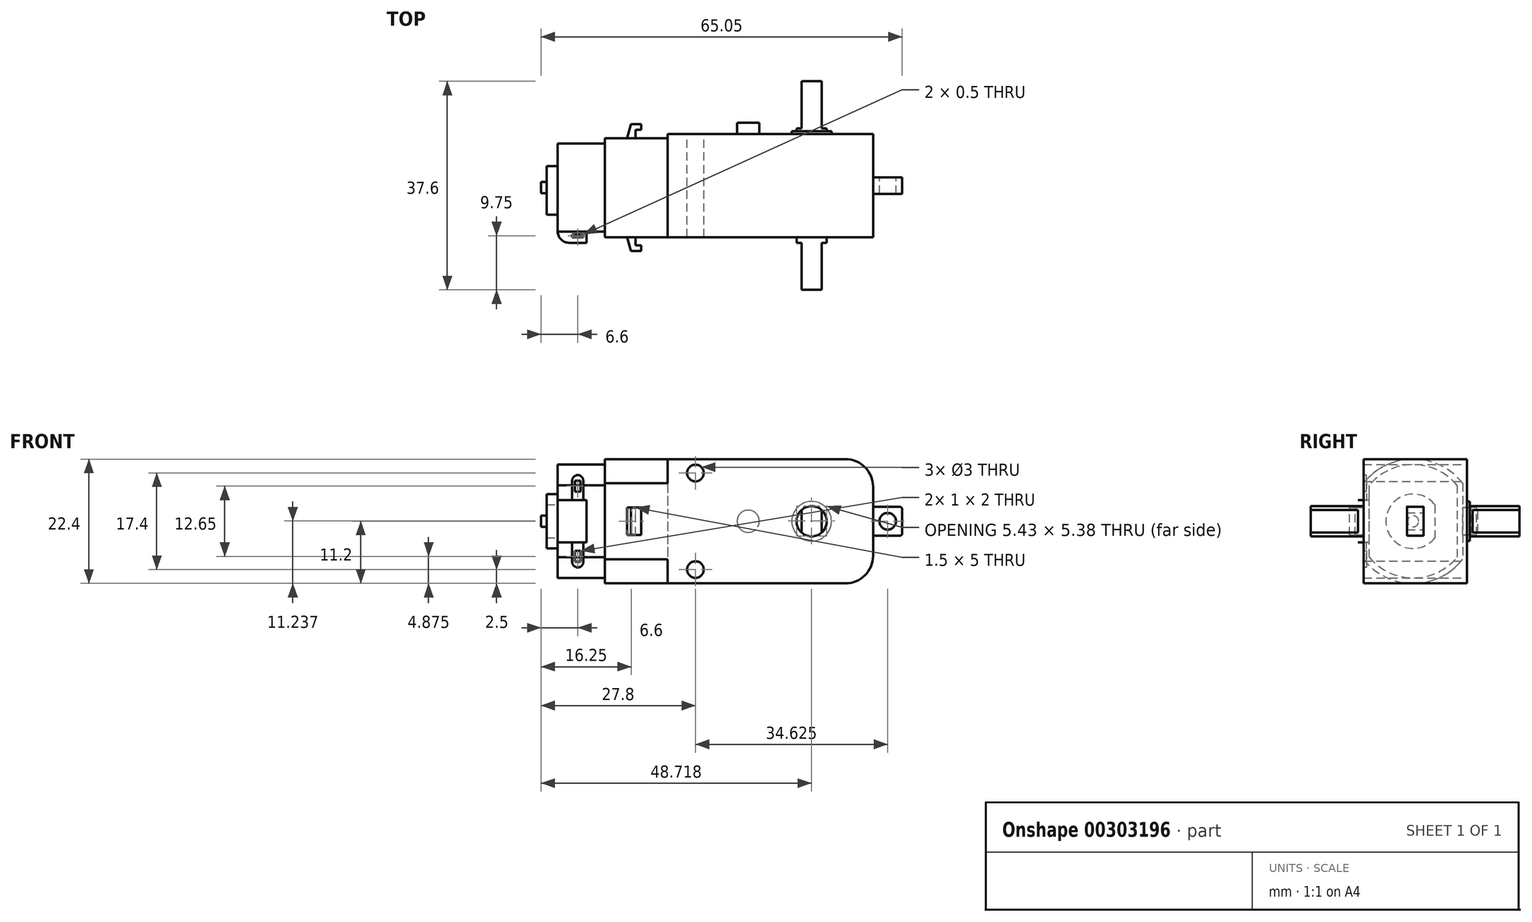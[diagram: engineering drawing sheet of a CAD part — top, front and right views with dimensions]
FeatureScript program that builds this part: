
annotation { "Feature Type Name" : "Feature", "Feature Type Description" : "" }
export const myFeature = defineFeature(function(context is Context, id is Id, definition is map)
    precondition{}
    {
        {
            var Q0;
            Q0=qCreatedBy(makeId("Top.planeOp"),FACE);
            var sketch = newSketch(context, id + "F0", { "sketchPlane" : qUnion([Q0])});
            skLineSegment(sketch, "E0.bottom", {"start": v(18.5, -9.3) * mm, "end": v(-18.5, -9.3) * mm});
            skLineSegment(sketch, "E0.top", {"start": v(18.5, 9.3) * mm, "end": v(-18.5, 9.3) * mm});
            skLineSegment(sketch, "E0.left", {"start": v(18.5, -9.3) * mm, "end": v(18.5, 9.3) * mm});
            skLineSegment(sketch, "E0.right", {"start": v(-18.5, -9.3) * mm, "end": v(-18.5, 9.3) * mm});
            skPoint(sketch, "E0.middle", {"position": v(0, 0) * mm});
            skSolve(sketch);
        }
        {
            var Q0;
            Q0 = qSketchRegion(id + "F0", true);
            extrude(context, id + "F1", {"entities" : qUnion([Q0]), "depth" : 22.4 * mm});
        }
        {
            var Q0;
            Q0=makeQuery(id+"F1.opExtrude","SWEPT_FACE",FACE,{"disambiguationData":[OSD([sQuery(id+"F0.wireOp",EDGE,"E0.right")])]});
            var sketch = newSketch(context, id + "F2", { "sketchPlane" : qUnion([Q0])});
            skLineSegment(sketch, "E1.0.1", {"start": v(9.3, 4.35) * mm, "end": v(9.3, 18.05) * mm});
            skLineSegment(sketch, "E1.0.2", {"start": v(0.38, 22.4) * mm, "end": v(0.38, 22.4) * mm});
            skLineSegment(sketch, "E1.0.3", {"start": v(-9.3, 22.4) * mm, "end": v(-9.3, 0) * mm, "construction": true});
            skLineSegment(sketch, "E2", {"start": v(-8.55, 18.05) * mm, "end": v(-8.55, 4.35) * mm});
            skLineSegment(sketch, "E3", {"start": v(-8.55, 11.2) * mm, "end": v(9.3, 11.2) * mm, "construction": true});
            skLineSegment(sketch, "E4", {"start": v(0.38, 11.2) * mm, "end": v(0.38, 22.4) * mm, "construction": true});
            skArc(sketch, "E5", {"start": v(9.3, 18.05) * mm, "mid": v(0.38, 22.4) * mm, "end": v(-8.55, 18.05) * mm});
            skArc(sketch, "E6.MirrorC", {"start": v(9.3, 4.35) * mm, "mid": v(0.38, 0) * mm, "end": v(-8.55, 4.35) * mm});
            skPoint(sketch, "E7.orphan", {"position": v(-8.55, 0) * mm});
            skPoint(sketch, "E8.orphan", {"position": v(9.3, 0) * mm});
            skPoint(sketch, "E9.orphan", {"position": v(9.3, 22.4) * mm});
            skPoint(sketch, "E10.orphan", {"position": v(-8.55, 22.4) * mm});
            skLineSegment(sketch, "E11", {"start": v(0.38, 11.2) * mm, "end": v(0.38, 0) * mm, "construction": true});
            skSolve(sketch);
        }
        {
            var Q0;
            Q0 = qSketchRegion(id + "F2", true);
            extrude(context, id + "F3", {"entities" : qUnion([Q0]), "operationType" : NewBodyOperationType.ADD, "depth" : 11.3 * mm});
        }
        {
            var Q0;
            Q0=makeQuery(id+"F3.opExtrude","CAP_FACE",FACE,{"disambiguationData":[OSD([sQuery(id+"F2.wireOp",EDGE,"E1.0.1"),sQuery(id+"F2.wireOp",EDGE,"E2"),sQuery(id+"F2.wireOp",EDGE,"E5"),sQuery(id+"F2.wireOp",EDGE,"E6.MirrorC")])],"isStart":false});
            var sketch = newSketch(context, id + "F4", { "sketchPlane" : qUnion([Q0])});
            skArc(sketch, "E12.0", {"start": v(-7.55, 4.7) * mm, "mid": v(0.38, 1) * mm, "end": v(8.3, 4.7) * mm});
            skLineSegment(sketch, "E12.1", {"start": v(-7.55, 17.7) * mm, "end": v(-7.55, 4.7) * mm});
            skArc(sketch, "E12.2", {"start": v(8.3, 17.7) * mm, "mid": v(0.38, 21.4) * mm, "end": v(-7.55, 17.7) * mm});
            skLineSegment(sketch, "E12.3", {"start": v(8.3, 4.7) * mm, "end": v(8.3, 17.7) * mm});
            skSolve(sketch);
        }
        {
            var Q0;
            Q0 = qSketchRegion(id + "F4", true);
            extrude(context, id + "F5", {"entities" : qUnion([Q0]), "operationType" : NewBodyOperationType.ADD, "depth" : 8.5 * mm});
        }
        {
            var Q0;
            Q0=makeQuery(id+"F5.opExtrude","CAP_FACE",FACE,{"disambiguationData":[OSD([sQuery(id+"F4.wireOp",EDGE,"E12.0"),sQuery(id+"F4.wireOp",EDGE,"E12.1"),sQuery(id+"F4.wireOp",EDGE,"E12.2"),sQuery(id+"F4.wireOp",EDGE,"E12.3")])],"isStart":false});
            var sketch = newSketch(context, id + "F6", { "sketchPlane" : qUnion([Q0])});
            skArc(sketch, "E13.0.0", {"start": v(-7.55, 4.7) * mm, "mid": v(0.38, 1) * mm, "end": v(8.3, 4.7) * mm, "construction": true});
            skLineSegment(sketch, "E13.0.1", {"start": v(8.3, 4.7) * mm, "end": v(8.3, 17.7) * mm, "construction": true});
            skArc(sketch, "E13.0.2", {"start": v(8.3, 17.7) * mm, "mid": v(0.38, 21.4) * mm, "end": v(-7.55, 17.7) * mm, "construction": true});
            skLineSegment(sketch, "E13.0.3", {"start": v(-7.55, 17.7) * mm, "end": v(-7.55, 4.7) * mm, "construction": true});
            skLineSegment(sketch, "E14", {"start": v(0.38, 11.07) * mm, "end": v(0.38, 11.33) * mm, "construction": true});
            skArc(sketch, "E15", {"start": v(-3.52, 8.23) * mm, "mid": v(5.28, 11.2) * mm, "end": v(-3.52, 14.17) * mm});
            skLineSegment(sketch, "E16", {"start": v(-3.52, 14.17) * mm, "end": v(-3.52, 8.23) * mm});
            skSolve(sketch);
        }
        {
            var Q0;
            Q0 = qSketchRegion(id + "F6", true);
            extrude(context, id + "F7", {"entities" : qUnion([Q0]), "operationType" : NewBodyOperationType.ADD, "depth" : 2 * mm});
        }
        {
            var Q0;
            Q0=makeQuery(id+"F7.opExtrude","CAP_FACE",FACE,{"disambiguationData":[OSD([sQuery(id+"F6.wireOp",EDGE,"E15"),sQuery(id+"F6.wireOp",EDGE,"E16")])],"isStart":false});
            var sketch = newSketch(context, id + "F8", { "sketchPlane" : qUnion([Q0])});
            skArc(sketch, "E17.0.0", {"start": v(-3.52, 8.23) * mm, "mid": v(5.28, 11.2) * mm, "end": v(-3.52, 14.17) * mm, "construction": true});
            skLineSegment(sketch, "E17.0.1", {"start": v(-3.52, 14.17) * mm, "end": v(-3.52, 8.23) * mm, "construction": true});
            skCircle(sketch, "E18", {"center": v(0.38, 11.2) * mm, "radius": 1 * mm});
            skSolve(sketch);
        }
        {
            var Q0;
            Q0 = qSketchRegion(id + "F8", true);
            extrude(context, id + "F9", {"entities" : qUnion([Q0]), "operationType" : NewBodyOperationType.ADD, "depth" : 1 * mm});
        }
        {
            var Q0;
            Q0=makeQuery(id+"F1.opExtrude","SWEPT_FACE",FACE,{"disambiguationData":[OSD([sQuery(id+"F0.wireOp",EDGE,"E0.top")])]});
            var sketch = newSketch(context, id + "F10", { "sketchPlane" : qUnion([Q0])});
            skLineSegment(sketch, "E19", {"start": v(-11, 22.4) * mm, "end": v(-11, 0) * mm, "construction": true});
            skLineSegment(sketch, "E20", {"start": v(-18.5, 11.2) * mm, "end": v(18.5, 11.2) * mm, "construction": true});
            skCircle(sketch, "E21", {"center": v(-7.42, 11.2) * mm, "radius": 3.58 * mm});
            skSolve(sketch);
        }
        {
            var Q0;
            Q0 = qSketchRegion(id + "F10", true);
            extrude(context, id + "F11", {"entities" : qUnion([Q0]), "operationType" : NewBodyOperationType.ADD, "depth" : 0.5 * mm, "hasSecondDirection" : true, "secondDirectionOppositeDirection" : true, "secondDirectionDepth" : 19.1 * mm});
        }
        {
            var Q0;
            Q0=makeQuery(id+"F11.opExtrude","CAP_FACE",FACE,{"disambiguationData":[OSD([sQuery(id+"F10.wireOp",EDGE,"E21")])],"isStart":false});
            var sketch = newSketch(context, id + "F12", { "sketchPlane" : qUnion([Q0])});
            skCircle(sketch, "E22.0.0", {"center": v(-7.42, 11.2) * mm, "radius": 3.58 * mm, "construction": true});
            skArc(sketch, "E23", {"start": v(-5.6, 13.22) * mm, "mid": v(-7.42, 13.92) * mm, "end": v(-9.25, 13.22) * mm});
            skLineSegment(sketch, "E24", {"start": v(-5.6, 13.22) * mm, "end": v(-5.6, 9.18) * mm});
            skLineSegment(sketch, "E25", {"start": v(-9.25, 13.22) * mm, "end": v(-9.25, 9.18) * mm});
            skArc(sketch, "E26.trimOffspring", {"start": v(-9.25, 9.18) * mm, "mid": v(-7.42, 8.47) * mm, "end": v(-5.6, 9.18) * mm});
            skSolve(sketch);
        }
        {
            var Q0;
            Q0 = qSketchRegion(id + "F12", true);
            extrude(context, id + "F13", {"entities" : qUnion([Q0]), "operationType" : NewBodyOperationType.ADD, "depth" : 9 * mm, "hasSecondDirection" : true, "secondDirectionOppositeDirection" : true, "secondDirectionDepth" : (19.6 + 9) * mm});
        }
        {
            var Q0;
            Q0=makeQuery(id+"F1.opExtrude","CAP_EDGE",EDGE,{"disambiguationData":[OSD([sQuery(id+"F0.wireOp",EDGE,"E0.left")])],"isStart":true});
            var Q1;
            Q1=makeQuery(id+"F1.opExtrude","CAP_EDGE",EDGE,{"disambiguationData":[OSD([sQuery(id+"F0.wireOp",EDGE,"E0.left")])],"isStart":false});
            fillet(context, id + "F14", {"entities" : qUnion([Q0, Q1]), "radius" : 5 * mm, "tangentPropagation" : true, "allowEdgeOverflow" : false});
        }
        {
            var Q0;
            Q0=makeQuery(id+"F1.opExtrude","SWEPT_FACE",FACE,{"disambiguationData":[OSD([sQuery(id+"F0.wireOp",EDGE,"E0.top")])]});
            var sketch = newSketch(context, id + "F15", { "sketchPlane" : qUnion([Q0])});
            skLineSegment(sketch, "E27", {"start": v(-18.5, 11.2) * mm, "end": v(-30.58, 11.2) * mm, "construction": true});
            skCircle(sketch, "E28", {"center": v(-21.12, 11.2) * mm, "radius": 1.5 * mm});
            skLineSegment(sketch, "E29", {"start": v(-18.5, 13.83) * mm, "end": v(-23.75, 13.83) * mm});
            skLineSegment(sketch, "E30", {"start": v(-18.5, 8.57) * mm, "end": v(-23.75, 8.57) * mm});
            skLineSegment(sketch, "E31", {"start": v(-23.75, 13.83) * mm, "end": v(-23.75, 8.57) * mm});
            skLineSegment(sketch, "E32", {"start": v(-18.5, 13.83) * mm, "end": v(-18.5, 8.57) * mm});
            skLineSegment(sketch, "E33", {"start": v(-21.12, 13.83) * mm, "end": v(-21.12, 8.57) * mm, "construction": true});
            skSolve(sketch);
        }
        {
            var Q0;
            Q0 = qSketchRegion(id + "F15", true);
            extrude(context, id + "F16", {"entities" : qUnion([Q0]), "operationType" : NewBodyOperationType.ADD, "oppositeDirection" : true, "depth" : (7.8 + 3) * mm, "hasSecondDirection" : true, "secondDirectionOppositeDirection" : true, "secondDirectionDepth" : 7.8 * mm});
        }
        {
            var Q0;
            Q0=makeQuery(id+"F16.opExtrude","SWEPT_EDGE",EDGE,{"disambiguationData":[OSD([sQuery(id+"F15.wireOp",EDGE,"E29"),sQuery(id+"F15.wireOp",EDGE,"E31")])]});
            var Q1;
            Q1=makeQuery(id+"F16.opExtrude","SWEPT_EDGE",EDGE,{"disambiguationData":[OSD([sQuery(id+"F0.wireOp",EDGE,"E0.top"),sQuery(id+"F0.wireOp",EDGE,"E0.left"),sQuery(id+"F15.wireOp",EDGE,"E29"),sQuery(id+"F15.wireOp",EDGE,"E32")])]});
            var Q2;
            Q2=makeQuery(id+"F16.opExtrude","SWEPT_EDGE",EDGE,{"disambiguationData":[OSD([sQuery(id+"F15.wireOp",EDGE,"E30"),sQuery(id+"F15.wireOp",EDGE,"E31")])]});
            var Q3;
            Q3=makeQuery(id+"F16.opExtrude","SWEPT_EDGE",EDGE,{"disambiguationData":[OSD([sQuery(id+"F0.wireOp",EDGE,"E0.top"),sQuery(id+"F0.wireOp",EDGE,"E0.left"),sQuery(id+"F15.wireOp",EDGE,"E30"),sQuery(id+"F15.wireOp",EDGE,"E32")])]});
            fillet(context, id + "F17", {"entities" : qUnion([Q0, Q1, Q2, Q3]), "radius" : 0.5 * mm, "tangentPropagation" : true, "allowEdgeOverflow" : false});
        }
        {
            var Q0;
            Q0=makeQuery(id+"F1.opExtrude","CAP_FACE",FACE,{"disambiguationData":[OSD([sQuery(id+"F0.wireOp",EDGE,"E0.bottom"),sQuery(id+"F0.wireOp",EDGE,"E0.top"),sQuery(id+"F0.wireOp",EDGE,"E0.left"),sQuery(id+"F0.wireOp",EDGE,"E0.right")])],"isStart":false});
            var sketch = newSketch(context, id + "F18", { "sketchPlane" : qUnion([Q0])});
            skLineSegment(sketch, "E34.0", {"start": v(-25.8, 8.55) * mm, "end": v(-24.3, 8.55) * mm});
            skLineSegment(sketch, "E35", {"start": v(-25.8, 8.55) * mm, "end": v(-25.13, 11.05) * mm});
            skLineSegment(sketch, "E36", {"start": v(-25.13, 11.05) * mm, "end": v(-23.3, 11.05) * mm});
            skLineSegment(sketch, "E37", {"start": v(-23.3, 11.05) * mm, "end": v(-23.3, 10.05) * mm});
            skLineSegment(sketch, "E38", {"start": v(-23.3, 10.05) * mm, "end": v(-24.3, 10.05) * mm});
            skLineSegment(sketch, "E39", {"start": v(-24.3, 10.05) * mm, "end": v(-24.3, 8.55) * mm});
            skPoint(sketch, "E40.orphan", {"position": v(-18.5, 8.55) * mm});
            skPoint(sketch, "E41.orphan", {"position": v(-29.8, 8.55) * mm});
            skLineSegment(sketch, "E42.0", {"start": v(-41.3, -1.38) * mm, "end": v(-41.3, 0.62) * mm, "construction": true});
            skLineSegment(sketch, "E43", {"start": v(-41.3, -0.38) * mm, "end": v(16.84, -0.38) * mm, "construction": true});
            skLineSegment(sketch, "E44.MirrorCS", {"start": v(-24.3, -10.8) * mm, "end": v(-24.3, -9.3) * mm});
            skLineSegment(sketch, "E45.MirrorCS", {"start": v(-23.3, -10.8) * mm, "end": v(-24.3, -10.8) * mm});
            skLineSegment(sketch, "E46.MirrorCS", {"start": v(-23.3, -11.8) * mm, "end": v(-23.3, -10.8) * mm});
            skLineSegment(sketch, "E47.MirrorCS", {"start": v(-25.8, -9.3) * mm, "end": v(-24.3, -9.3) * mm});
            skPoint(sketch, "E48.MirrorP", {"position": v(-29.8, -9.3) * mm});
            skPoint(sketch, "E49.MirrorP", {"position": v(-18.5, -9.3) * mm});
            skLineSegment(sketch, "E50.MirrorCS", {"start": v(-25.13, -11.8) * mm, "end": v(-23.3, -11.8) * mm});
            skLineSegment(sketch, "E51.MirrorCS", {"start": v(-25.8, -9.3) * mm, "end": v(-25.13, -11.8) * mm});
            skSolve(sketch);
        }
        {
            var Q0;
            Q0 = qSketchRegion(id + "F18", true);
            extrude(context, id + "F19", {"entities" : qUnion([Q0]), "operationType" : NewBodyOperationType.ADD, "oppositeDirection" : true, "depth" : (11.2 + 2.5) * mm, "hasSecondDirection" : true, "secondDirectionOppositeDirection" : true, "secondDirectionDepth" : (11.2 - 2.5) * mm});
        }
        {
            var Q0;
            Q0=makeQuery(id+"F1.opExtrude","SWEPT_FACE",FACE,{"disambiguationData":[OSD([sQuery(id+"F0.wireOp",EDGE,"E0.top")])]});
            var sketch = newSketch(context, id + "F20", { "sketchPlane" : qUnion([Q0])});
            skLineSegment(sketch, "E52.0.0", {"start": v(-18.5, 17.4) * mm, "end": v(-18.5, 5) * mm, "construction": true});
            skArc(sketch, "E52.0.1", {"start": v(-18.5, 5) * mm, "mid": v(-17.04, 1.46) * mm, "end": v(-13.5, 0) * mm, "construction": true});
            skLineSegment(sketch, "E52.0.2", {"start": v(-13.5, 0) * mm, "end": v(18.5, 0) * mm, "construction": true});
            skLineSegment(sketch, "E52.0.3", {"start": v(18.5, 0) * mm, "end": v(18.5, 22.4) * mm, "construction": true});
            skLineSegment(sketch, "E52.0.4", {"start": v(18.5, 22.4) * mm, "end": v(-13.5, 22.4) * mm, "construction": true});
            skArc(sketch, "E52.0.5", {"start": v(-13.5, 22.4) * mm, "mid": v(-17.04, 20.94) * mm, "end": v(-18.5, 17.4) * mm, "construction": true});
            skLineSegment(sketch, "E53", {"start": v(18.5, 11.2) * mm, "end": v(4, 11.2) * mm, "construction": true});
            skCircle(sketch, "E54", {"center": v(4, 11.2) * mm, "radius": 2 * mm});
            skSolve(sketch);
        }
        {
            var Q0;
            Q0 = qSketchRegion(id + "F20", true);
            extrude(context, id + "F21", {"entities" : qUnion([Q0]), "operationType" : NewBodyOperationType.ADD, "depth" : 2 * mm});
        }
        {
            var Q0;
            Q0=makeQuery(id+"F1.opExtrude","SWEPT_FACE",FACE,{"disambiguationData":[OSD([sQuery(id+"F0.wireOp",EDGE,"E0.top")])]});
            var sketch = newSketch(context, id + "F22", { "sketchPlane" : qUnion([Q0])});
            skLineSegment(sketch, "E55.0", {"start": v(-23.75, 13.32) * mm, "end": v(-23.75, 9.07) * mm, "construction": true});
            skLineSegment(sketch, "E56", {"start": v(-23.75, 11.2) * mm, "end": v(41.3, 11.2) * mm, "construction": true});
            skLineSegment(sketch, "E57.0", {"start": v(-13.5, 22.4) * mm, "end": v(18.5, 22.4) * mm, "construction": true});
            skCircle(sketch, "E58", {"center": v(13.5, 19.9) * mm, "radius": 1.5 * mm});
            skCircle(sketch, "E59.MirrorC", {"center": v(13.5, 2.5) * mm, "radius": 1.5 * mm});
            skSolve(sketch);
        }
        {
            var Q0;
            Q0 = qSketchRegion(id + "F22", true);
            extrude(context, id + "F23", {"entities" : qUnion([Q0]), "operationType" : NewBodyOperationType.REMOVE, "endBound" : BoundingType.THROUGH_ALL, "oppositeDirection" : true, "depth" : 25 * mm});
        }
        {
            var Q0;
            Q0=makeQuery(id+"F11.opExtrude","CAP_FACE",FACE,{"disambiguationData":[OSD([sQuery(id+"F10.wireOp",EDGE,"E21")])],"isStart":true});
            extrude(context, id + "F24", {"entities" : qUnion([Q0]), "operationType" : NewBodyOperationType.REMOVE, "oppositeDirection" : true, "depth" : 0.5 * mm});
        }
        {
            var Q0;
            Q0=makeQuery(id+"F24.boolean.opBoolean","MERGE",FACE,{"derivedFrom":[makeQuery(id+"F3.boolean.opBoolean","MERGE",FACE,{"derivedFrom":[makeQuery(id+"F1.opExtrude","SWEPT_FACE",FACE,{"disambiguationData":[OSD([sQuery(id+"F0.wireOp",EDGE,"E0.bottom")])]}),makeQuery(id+"F3.opExtrude","SWEPT_FACE",FACE,{"disambiguationData":[OSD([sQuery(id+"F2.wireOp",EDGE,"E1.0.1")])]})]}),makeQuery(id+"F24.opExtrude","CAP_FACE",FACE,{"disambiguationData":[OSD([sQuery(id+"F10.wireOp",EDGE,"E21")])],"isStart":false})]});
            var sketch = newSketch(context, id + "F25", { "sketchPlane" : qUnion([Q0])});
            skLineSegment(sketch, "E60.0.0", {"start": v(9.25, 9.18) * mm, "end": v(9.25, 13.22) * mm, "construction": true});
            skArc(sketch, "E60.0.1", {"start": v(9.25, 13.22) * mm, "mid": v(7.42, 13.92) * mm, "end": v(5.6, 13.22) * mm, "construction": true});
            skLineSegment(sketch, "E60.0.2", {"start": v(5.6, 13.22) * mm, "end": v(5.6, 9.18) * mm, "construction": true});
            skArc(sketch, "E60.0.3", {"start": v(5.6, 9.18) * mm, "mid": v(7.42, 8.47) * mm, "end": v(9.25, 9.18) * mm, "construction": true});
            skCircle(sketch, "E61", {"center": v(7.43, 11.2) * mm, "radius": 2.72 * mm});
            skSolve(sketch);
        }
        {
            var Q0;
            Q0 = qSketchRegion(id + "F25", true);
            extrude(context, id + "F26", {"entities" : qUnion([Q0]), "operationType" : NewBodyOperationType.ADD, "depth" : 1 * mm, "hasSecondDirection" : true, "secondDirectionOppositeDirection" : true, "secondDirectionDepth" : 19.6 * mm});
        }
        {
            var Q0;
            Q0=makeQuery(id+"F5.opExtrude","SWEPT_FACE",FACE,{"disambiguationData":[OSD([sQuery(id+"F4.wireOp",EDGE,"E12.3")])]});
            var sketch = newSketch(context, id + "F27", { "sketchPlane" : qUnion([Q0])});
            skLineSegment(sketch, "E62.0", {"start": v(-38.3, 7.38) * mm, "end": v(-38.3, 15.03) * mm});
            skLineSegment(sketch, "E63", {"start": v(-38.3, 11.2) * mm, "end": v(-29.8, 11.2) * mm, "construction": true});
            skLineSegment(sketch, "E64.bottom", {"start": v(-38.3, 7.38) * mm, "end": v(-33.1, 7.38) * mm});
            skLineSegment(sketch, "E64.top", {"start": v(-38.3, 15.03) * mm, "end": v(-33.1, 15.03) * mm});
            skLineSegment(sketch, "E64.right", {"start": v(-33.1, 7.38) * mm, "end": v(-33.1, 15.03) * mm});
            skPoint(sketch, "E65.orphan", {"position": v(-38.3, 17.7) * mm});
            skPoint(sketch, "E66.orphan", {"position": v(-38.3, 4.7) * mm});
            skSolve(sketch);
        }
        {
            var Q0;
            Q0 = qSketchRegion(id + "F27", true);
            extrude(context, id + "F28", {"entities" : qUnion([Q0]), "operationType" : NewBodyOperationType.ADD, "depth" : 2 * mm});
        }
        {
            var Q0;
            Q0=makeQuery(id+"F28.opExtrude","CAP_EDGE",EDGE,{"disambiguationData":[OSD([sQuery(id+"F27.wireOp",EDGE,"E62.0")])],"isStart":false});
            fillet(context, id + "F29", {"entities" : qUnion([Q0]), "radius" : 2 * mm, "tangentPropagation" : true, "allowEdgeOverflow" : false});
        }
        {
            var Q0;
            Q0=makeQuery(id+"F28.opExtrude","CAP_FACE",FACE,{"disambiguationData":[OSD([sQuery(id+"F27.wireOp",EDGE,"E64.bottom"),sQuery(id+"F27.wireOp",EDGE,"E64.top"),sQuery(id+"F27.wireOp",EDGE,"E62.0"),sQuery(id+"F27.wireOp",EDGE,"E64.right")])],"isStart":false});
            var sketch = newSketch(context, id + "F30", { "sketchPlane" : qUnion([Q0])});
            skLineSegment(sketch, "E67.0", {"start": v(-35.7, 15.03) * mm, "end": v(-33.7, 15.03) * mm});
            skLineSegment(sketch, "E68", {"start": v(-33.1, 11.2) * mm, "end": v(-41.3, 11.2) * mm, "construction": true});
            skPoint(sketch, "E68.endSnap0", {"position": v(-33.1, 11.2) * mm});
            skLineSegment(sketch, "E69", {"start": v(-34.7, 15.03) * mm, "end": v(-34.7, 18.52) * mm, "construction": true});
            skArc(sketch, "E70", {"start": v(-33.7, 18.52) * mm, "mid": v(-34.7, 19.53) * mm, "end": v(-35.7, 18.52) * mm});
            skLineSegment(sketch, "E71", {"start": v(-33.7, 18.52) * mm, "end": v(-33.7, 15.03) * mm});
            skLineSegment(sketch, "E72.MirrorCS", {"start": v(-35.7, 18.52) * mm, "end": v(-35.7, 15.03) * mm});
            skLineSegment(sketch, "E73.bottom", {"start": v(-34.2, 16.52) * mm, "end": v(-35.2, 16.52) * mm});
            skLineSegment(sketch, "E73.top", {"start": v(-34.2, 18.52) * mm, "end": v(-35.2, 18.52) * mm});
            skLineSegment(sketch, "E73.left", {"start": v(-34.2, 16.52) * mm, "end": v(-34.2, 18.52) * mm});
            skLineSegment(sketch, "E73.right", {"start": v(-35.2, 16.52) * mm, "end": v(-35.2, 18.52) * mm});
            skPoint(sketch, "E73.middle", {"position": v(-34.7, 17.52) * mm});
            skPoint(sketch, "E74.orphan", {"position": v(-33.1, 15.03) * mm});
            skPoint(sketch, "E75.orphan", {"position": v(-36.3, 15.03) * mm});
            skLineSegment(sketch, "E76.MirrorCS", {"start": v(-35.2, 18.52) * mm, "end": v(-34.2, 18.52) * mm});
            skLineSegment(sketch, "E77.MirrorCS", {"start": v(-33.7, 15.03) * mm, "end": v(-35.7, 15.03) * mm});
            skArc(sketch, "E78.MirrorCS", {"start": v(-35.7, 18.52) * mm, "mid": v(-34.7, 19.53) * mm, "end": v(-33.7, 18.52) * mm});
            skLineSegment(sketch, "E79.MirrorCS", {"start": v(-35.2, 16.52) * mm, "end": v(-34.2, 16.52) * mm});
            skLineSegment(sketch, "E80.MirrorCS", {"start": v(-34.2, 3.88) * mm, "end": v(-35.2, 3.88) * mm});
            skLineSegment(sketch, "E81.MirrorCS", {"start": v(-35.2, 3.88) * mm, "end": v(-34.2, 3.88) * mm});
            skLineSegment(sketch, "E82.MirrorCS", {"start": v(-34.2, 5.88) * mm, "end": v(-34.2, 3.88) * mm});
            skLineSegment(sketch, "E83.MirrorCS", {"start": v(-35.7, 3.88) * mm, "end": v(-35.7, 7.38) * mm});
            skLineSegment(sketch, "E84.MirrorCS", {"start": v(-33.7, 3.88) * mm, "end": v(-33.7, 7.38) * mm});
            skLineSegment(sketch, "E85.MirrorCS", {"start": v(-34.2, 5.88) * mm, "end": v(-35.2, 5.88) * mm});
            skArc(sketch, "E86.MirrorCS", {"start": v(-35.7, 3.88) * mm, "mid": v(-34.7, 2.88) * mm, "end": v(-33.7, 3.88) * mm});
            skLineSegment(sketch, "E87.MirrorCS", {"start": v(-33.7, 7.38) * mm, "end": v(-35.7, 7.38) * mm});
            skLineSegment(sketch, "E88.MirrorCS", {"start": v(-35.2, 5.88) * mm, "end": v(-34.2, 5.88) * mm});
            skPoint(sketch, "E89.MirrorP", {"position": v(-36.3, 7.38) * mm});
            skPoint(sketch, "E90.MirrorP", {"position": v(-33.1, 7.38) * mm});
            skLineSegment(sketch, "E91.MirrorCS", {"start": v(-35.2, 5.88) * mm, "end": v(-35.2, 3.88) * mm});
            skPoint(sketch, "E92.MirrorP", {"position": v(-34.7, 4.88) * mm});
            skLineSegment(sketch, "E93.MirrorCS", {"start": v(-34.7, 7.38) * mm, "end": v(-34.7, 3.88) * mm, "construction": true});
            skLineSegment(sketch, "E94.MirrorCS", {"start": v(-35.7, 7.38) * mm, "end": v(-33.7, 7.38) * mm});
            skArc(sketch, "E95.MirrorCS", {"start": v(-33.7, 3.88) * mm, "mid": v(-34.7, 2.88) * mm, "end": v(-35.7, 3.88) * mm});
            skSolve(sketch);
        }
        {
            var Q0;
            Q0 = qSketchRegion(id + "F30", true);
            extrude(context, id + "F31", {"entities" : qUnion([Q0]), "operationType" : NewBodyOperationType.ADD, "oppositeDirection" : true, "depth" : 1.5 * mm, "hasSecondDirection" : true, "secondDirectionOppositeDirection" : true, "secondDirectionDepth" : 1 * mm});
        }
    });
